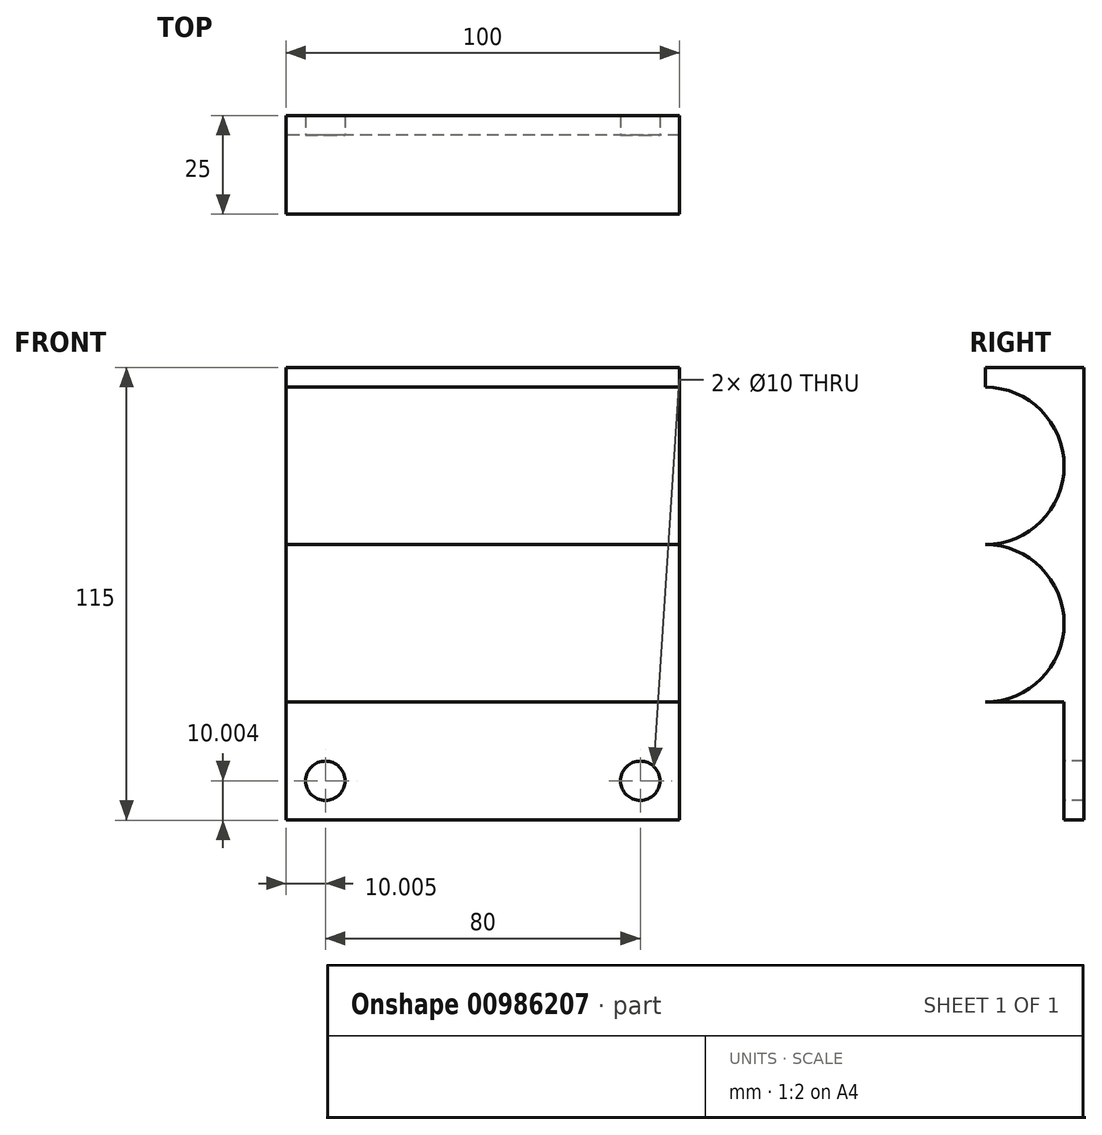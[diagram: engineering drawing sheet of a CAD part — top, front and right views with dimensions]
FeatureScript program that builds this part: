
annotation { "Feature Type Name" : "Feature", "Feature Type Description" : "" }
export const myFeature = defineFeature(function(context is Context, id is Id, definition is map)
    precondition{}
    {
        {
            var Q0;
            Q0=qCreatedBy(makeId("Front.planeOp"),FACE);
            var sketch = newSketch(context, id + "F0", { "sketchPlane" : qUnion([Q0])});
            skLineSegment(sketch, "E0", {"start": v(-23.64, -55.47) * mm, "end": v(76.36, -55.47) * mm});
            skLineSegment(sketch, "E1", {"start": v(76.36, -55.47) * mm, "end": v(76.36, 24.53) * mm});
            skLineSegment(sketch, "E2", {"start": v(-23.64, -55.47) * mm, "end": v(-23.64, 24.53) * mm});
            skLineSegment(sketch, "E3", {"start": v(76.36, 24.53) * mm, "end": v(-23.64, 24.53) * mm});
            skSolve(sketch);
        }
        {
            var Q0;
            Q0 = qSketchRegion(id + "F0", true);
            extrude(context, id + "F1", {"entities" : qUnion([Q0]), "depth" : 5 * mm, "offsetDistance" : 25 * mm});
        }
        {
            var Q0;
            Q0=makeQuery(id+"F1.opExtrude","SWEPT_FACE",FACE,{"disambiguationData":[OSD([sQuery(id+"F0.wireOp",EDGE,"E1")])]});
            var sketch = newSketch(context, id + "F2", { "sketchPlane" : qUnion([Q0])});
            skArc(sketch, "E4", {"start": v(-25, -55.47) * mm, "mid": v(-5, -35.47) * mm, "end": v(-25, -15.47) * mm});
            skLineSegment(sketch, "E5", {"start": v(-5, 24.53) * mm, "end": v(-5, -55.47) * mm});
            skLineSegment(sketch, "E6", {"start": v(-5, 24.53) * mm, "end": v(-25, 24.53) * mm, "construction": true});
            skLineSegment(sketch, "E7", {"start": v(-25, -55.47) * mm, "end": v(-5, -55.47) * mm, "construction": true});
            skArc(sketch, "E8", {"start": v(-25, -15.47) * mm, "mid": v(-5, 4.53) * mm, "end": v(-25, 24.53) * mm});
            skLineSegment(sketch, "E9", {"start": v(-25, 24.53) * mm, "end": v(-25, -55.47) * mm, "construction": true});
            skLineSegment(sketch, "E10", {"start": v(-25, 24.53) * mm, "end": v(-5, 24.53) * mm});
            skLineSegment(sketch, "E11", {"start": v(-25, -55.47) * mm, "end": v(-5, -55.47) * mm});
            skPoint(sketch, "E12.start.orphan", {"position": v(-45, 24.53) * mm});
            skPoint(sketch, "E13.orphan", {"position": v(-45, -55.47) * mm});
            skSolve(sketch);
        }
        {
            var Q0;
            {var subQ0=sQuery(id+"F2.wireOp",EDGE,"E10");Q0=makeQuery(id+"F2.imprint","IMPRINT",FACE,{"disambiguationData":[TD([[makeQuery(id+"F2.imprint","IMPRINT",EDGE,{"derivedFrom":subQ0}),-1.0]])]});}
            var Q1;
            {var subQ0=sQuery(id+"F2.wireOp",EDGE,"E8");var subQ1=sQuery(id+"F2.wireOp",EDGE,"E4");var subQ2=makeQuery(id+"F2.imprint","INTERSECT",VERTEX,{"derivedFrom":[subQ1,subQ0]});Q1=makeQuery(id+"F2.imprint","IMPRINT",FACE,{"disambiguationData":[TD([[makeQuery(id+"F2.imprint","IMPRINT",EDGE,{"disambiguationData":[TD([[subQ2,1.0]])],"derivedFrom":subQ1}),-1.0]])]});}
            var Q2;
            {var subQ0=sQuery(id+"F2.wireOp",EDGE,"E11");Q2=makeQuery(id+"F2.imprint","IMPRINT",FACE,{"disambiguationData":[TD([[makeQuery(id+"F2.imprint","IMPRINT",EDGE,{"derivedFrom":subQ0}),1.0]])]});}
            extrude(context, id + "F3", {"entities" : qUnion([Q0, Q1, Q2]), "operationType" : NewBodyOperationType.ADD, "oppositeDirection" : true, "depth" : 100 * mm, "offsetDistance" : 25 * mm});
        }
        {
            var Q0;
            Q0=makeQuery(id+"F3.boolean.opBoolean","MERGE",FACE,{"derivedFrom":[makeQuery(id+"F1.opExtrude","SWEPT_FACE",FACE,{"disambiguationData":[OSD([sQuery(id+"F0.wireOp",EDGE,"E0")])]}),makeQuery(id+"F3.opExtrude","SWEPT_FACE",FACE,{"disambiguationData":[OSD([sQuery(id+"F2.wireOp",EDGE,"E11")])]})]});
            var sketch = newSketch(context, id + "F4", { "sketchPlane" : qUnion([Q0])});
            skLineSegment(sketch, "E14", {"start": v(-23.64, 0) * mm, "end": v(76.36, 0) * mm});
            skLineSegment(sketch, "E15", {"start": v(76.36, 0) * mm, "end": v(76.36, 5) * mm});
            skLineSegment(sketch, "E16", {"start": v(76.36, 5) * mm, "end": v(-23.64, 5) * mm});
            skLineSegment(sketch, "E17", {"start": v(-23.64, 5) * mm, "end": v(-23.64, 0) * mm});
            skSolve(sketch);
        }
        {
            var Q0;
            Q0=makeQuery(id+"F4.imprint","IMPRINT",FACE,{"disambiguationData":[TD([[makeQuery(id+"F4.imprint","IMPRINT",EDGE,{"derivedFrom":sQuery(id+"F4.wireOp",EDGE,"E14")}),1.0]])]});
            extrude(context, id + "F5", {"entities" : qUnion([Q0]), "operationType" : NewBodyOperationType.ADD, "depth" : 30 * mm, "offsetDistance" : 25 * mm});
        }
        {
            var Q0;
            Q0=makeQuery(id+"F5.opExtrude","SWEPT_FACE",FACE,{"disambiguationData":[OSD([sQuery(id+"F4.wireOp",EDGE,"E16")])]});
            var sketch = newSketch(context, id + "F6", { "sketchPlane" : qUnion([Q0])});
            skCircle(sketch, "E18", {"center": v(66.36, -75.47) * mm, "radius": 5 * mm});
            skCircle(sketch, "E19", {"center": v(-13.64, -75.47) * mm, "radius": 5 * mm});
            skSolve(sketch);
        }
        {
            var Q0;
            Q0 = qSketchRegion(id + "F6", true);
            extrude(context, id + "F7", {"entities" : qUnion([Q0]), "operationType" : NewBodyOperationType.REMOVE, "oppositeDirection" : true, "depth" : 5 * mm, "offsetDistance" : 25 * mm});
        }
        {
            var Q0;
            Q0=makeQuery(id+"F3.boolean.opBoolean","MERGE",FACE,{"derivedFrom":[makeQuery(id+"F1.opExtrude","SWEPT_FACE",FACE,{"disambiguationData":[OSD([sQuery(id+"F0.wireOp",EDGE,"E3")])]}),makeQuery(id+"F3.opExtrude","SWEPT_FACE",FACE,{"disambiguationData":[OSD([sQuery(id+"F2.wireOp",EDGE,"E10")])]})]});
            var sketch = newSketch(context, id + "F8", { "sketchPlane" : qUnion([Q0])});
            skLineSegment(sketch, "E20.bottom", {"start": v(-23.64, -25) * mm, "end": v(76.36, -25) * mm});
            skLineSegment(sketch, "E20.top", {"start": v(-23.64, 0) * mm, "end": v(76.36, 0) * mm});
            skLineSegment(sketch, "E20.left", {"start": v(-23.64, -25) * mm, "end": v(-23.64, 0) * mm});
            skLineSegment(sketch, "E20.right", {"start": v(76.36, -25) * mm, "end": v(76.36, 0) * mm});
            skSolve(sketch);
        }
        {
            var Q0;
            Q0=makeQuery(id+"F8.imprint","IMPRINT",FACE,{"disambiguationData":[TD([[makeQuery(id+"F8.imprint","IMPRINT",EDGE,{"derivedFrom":sQuery(id+"F8.wireOp",EDGE,"E20.bottom")}),1.0]])]});
            extrude(context, id + "F9", {"entities" : qUnion([Q0]), "operationType" : NewBodyOperationType.ADD, "depth" : 5 * mm, "offsetDistance" : 25 * mm});
        }
    });
